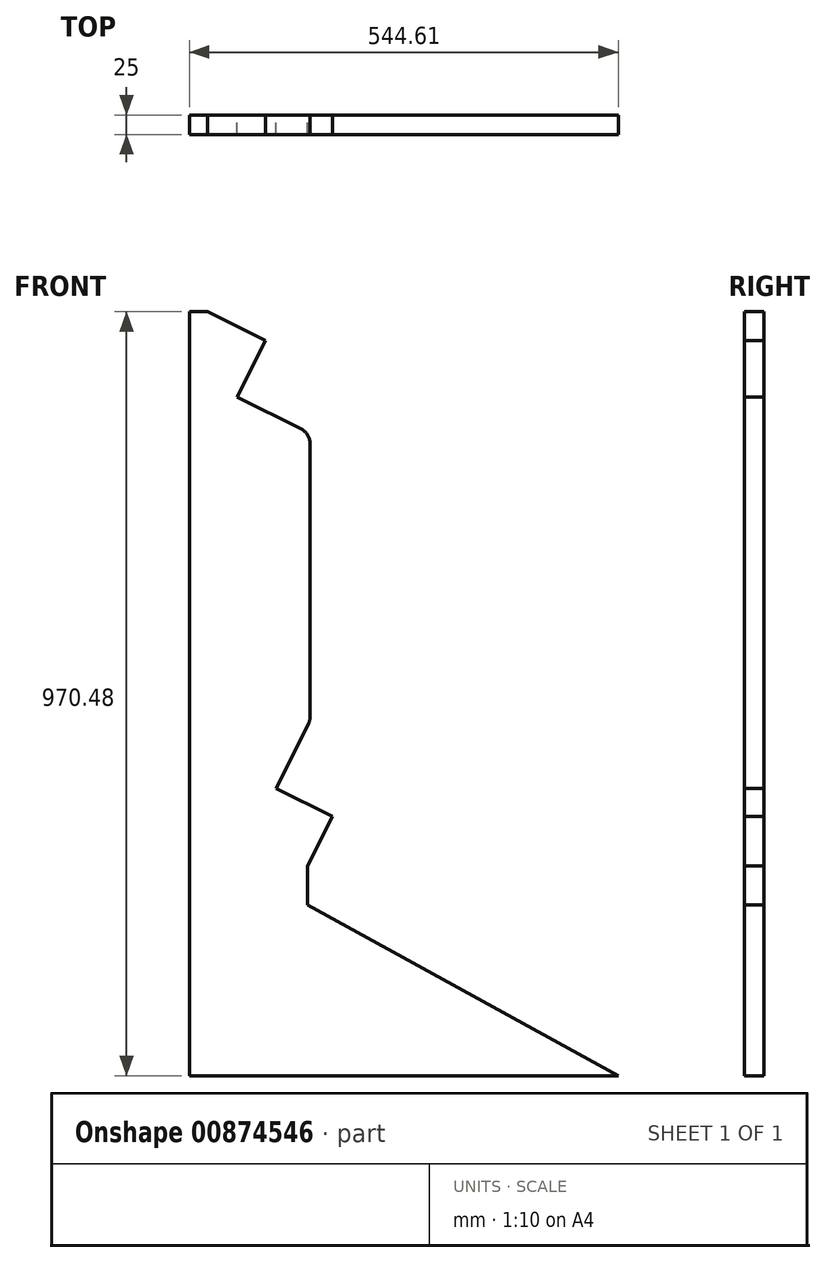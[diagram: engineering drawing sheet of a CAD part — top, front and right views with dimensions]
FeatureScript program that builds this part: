
annotation { "Feature Type Name" : "Feature", "Feature Type Description" : "" }
export const myFeature = defineFeature(function(context is Context, id is Id, definition is map)
    precondition{}
    {
        {
            var Q0;
            Q0=qCreatedBy(makeId("Front.planeOp"),FACE);
            var sketch = newSketch(context, id + "F0", { "sketchPlane" : qUnion([Q0])});
            skLineSegment(sketch, "E0", {"start": v(450.11, -616.7) * mm, "end": v(55.68, -400.08) * mm});
            skLineSegment(sketch, "E1", {"start": v(55.68, -400.08) * mm, "end": v(55.68, -350.08) * mm});
            skLineSegment(sketch, "E2", {"start": v(55.68, -350.08) * mm, "end": v(87.04, -287.5) * mm});
            skLineSegment(sketch, "E3", {"start": v(138.57, -161.03) * mm, "end": v(138.57, 186.73) * mm, "construction": true});
            skLineSegment(sketch, "E4", {"start": v(83.4, 276.12) * mm, "end": v(46.5, 294.62) * mm, "construction": true});
            skLineSegment(sketch, "E5", {"start": v(-94.5, 353.79) * mm, "end": v(-94.5, -616.7) * mm});
            skPoint(sketch, "E6.visualSharp", {"position": v(138.57, 248.45) * mm});
            skArc(sketch, "E6.filletArc", {"start": v(138.57, 186.73) * mm, "mid": v(123.67, 239.25) * mm, "end": v(83.4, 276.12) * mm, "construction": true});
            skPoint(sketch, "E7.visualSharp", {"position": v(138.57, -184.69) * mm});
            skArc(sketch, "E7.filletArc", {"start": v(127.97, -205.84) * mm, "mid": v(135.89, -184.05) * mm, "end": v(138.57, -161.03) * mm, "construction": true});
            skLineSegment(sketch, "E8", {"start": v(-107, 353.79) * mm, "end": v(-107, -616.7) * mm, "construction": true});
            skLineSegment(sketch, "E9", {"start": v(-94.5, -616.7) * mm, "end": v(450.11, -616.7) * mm});
            skLineSegment(sketch, "E10.0", {"start": v(69.95, 249.3) * mm, "end": v(33.05, 267.8) * mm, "construction": true});
            skLineSegment(sketch, "E10.1", {"start": v(82.63, -229.36) * mm, "end": v(101.15, -192.4) * mm, "construction": true});
            skArc(sketch, "E10.2", {"start": v(101.15, -192.4) * mm, "mid": v(106.7, -177.15) * mm, "end": v(108.57, -161.03) * mm, "construction": true});
            skLineSegment(sketch, "E10.3", {"start": v(108.57, -161.03) * mm, "end": v(108.57, 186.73) * mm, "construction": true});
            skArc(sketch, "E10.4", {"start": v(108.57, 186.73) * mm, "mid": v(98.14, 223.5) * mm, "end": v(69.95, 249.3) * mm, "construction": true});
            skLineSegment(sketch, "E11", {"start": v(46.5, 294.62) * mm, "end": v(33.05, 267.8) * mm, "construction": true});
            skLineSegment(sketch, "E12", {"start": v(-94.5, 353.79) * mm, "end": v(-71.5, 353.79) * mm});
            skLineSegment(sketch, "E13.0", {"start": v(87.04, -287.5) * mm, "end": v(15.52, -251.65) * mm});
            skLineSegment(sketch, "E13.1", {"start": v(15.52, -251.65) * mm, "end": v(56.45, -170) * mm});
            skArc(sketch, "E13.2", {"start": v(56.45, -170) * mm, "mid": v(58.04, -165.64) * mm, "end": v(58.57, -161.03) * mm});
            skLineSegment(sketch, "E13.3", {"start": v(1.8, 317.03) * mm, "end": v(-34.06, 245.52) * mm});
            skLineSegment(sketch, "E13.4", {"start": v(47.54, 204.6) * mm, "end": v(-34.06, 245.52) * mm});
            skArc(sketch, "E13.5", {"start": v(58.57, 186.73) * mm, "mid": v(55.6, 197.23) * mm, "end": v(47.54, 204.6) * mm});
            skLineSegment(sketch, "E13.6", {"start": v(58.57, -161.03) * mm, "end": v(58.57, 186.73) * mm});
            skLineSegment(sketch, "E14.trimOffspring", {"start": v(1.8, 317.03) * mm, "end": v(-71.5, 353.79) * mm});
            skLineSegment(sketch, "E15.trimOffspring", {"start": v(109.45, -242.8) * mm, "end": v(127.97, -205.84) * mm, "construction": true});
            skSolve(sketch);
        }
        {
            var Q0;
            Q0=makeQuery(id+"F0.imprint","IMPRINT",FACE,{"disambiguationData":[TD([[makeQuery(id+"F0.imprint","IMPRINT",EDGE,{"derivedFrom":sQuery(id+"F0.wireOp",EDGE,"E0")}),1.0]])]});
            extrude(context, id + "F1", {"entities" : qUnion([Q0]), "depth" : 25 * mm, "offsetDistance" : 25 * mm});
        }
    });
